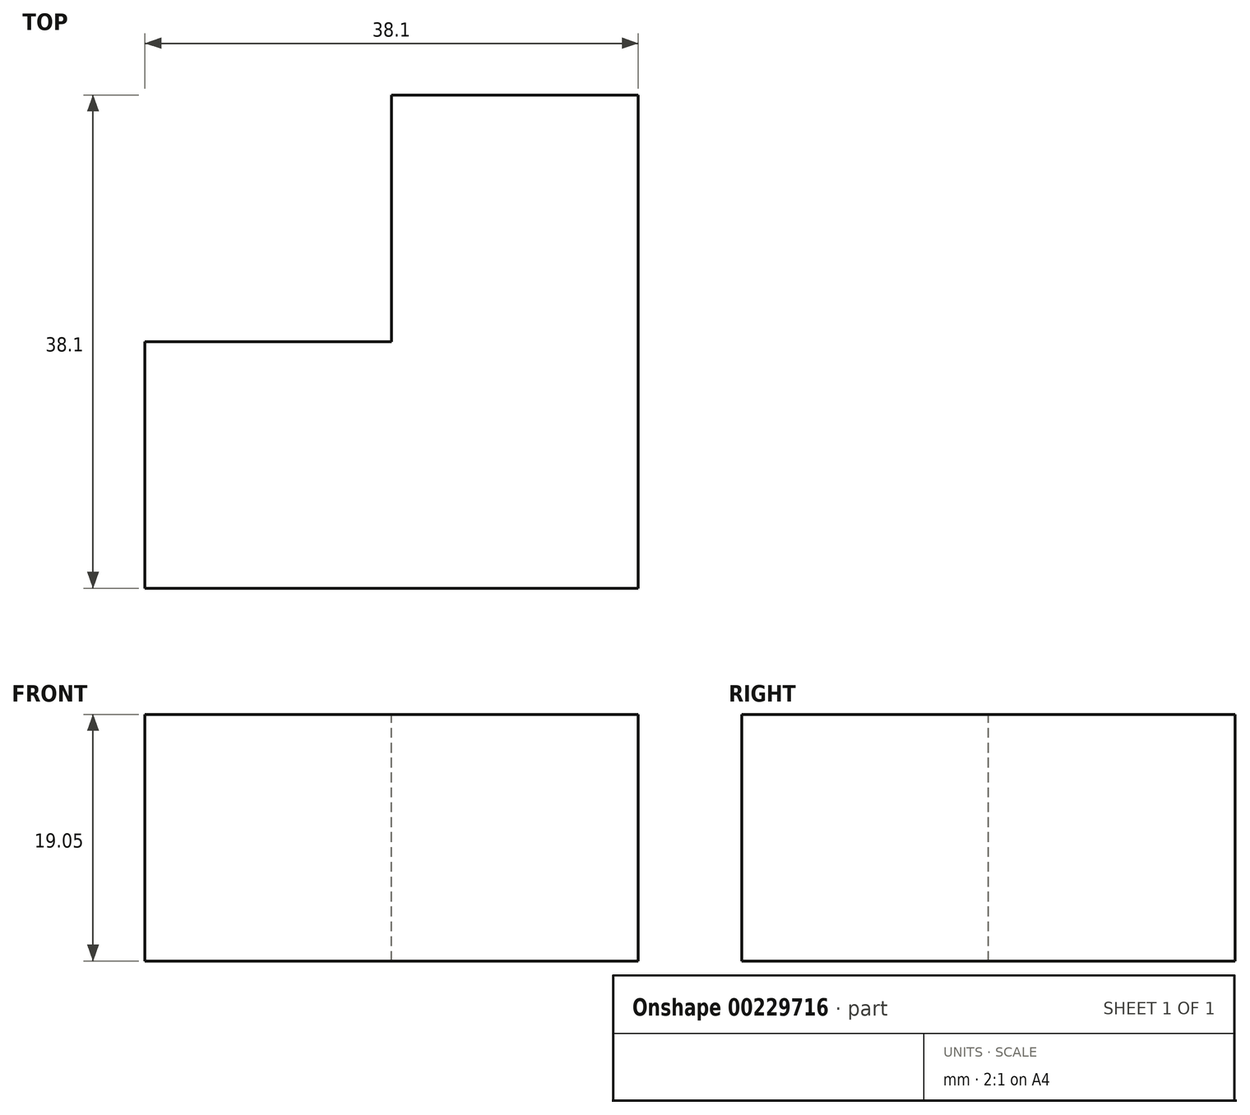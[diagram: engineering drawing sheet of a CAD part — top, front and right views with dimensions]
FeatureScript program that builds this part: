
annotation { "Feature Type Name" : "Feature", "Feature Type Description" : "" }
export const myFeature = defineFeature(function(context is Context, id is Id, definition is map)
    precondition{}
    {
        {
            var Q0;
            Q0=qCreatedBy(makeId("Front.planeOp"),FACE);
            var sketch = newSketch(context, id + "F0", { "sketchPlane" : qUnion([Q0])});
            skLineSegment(sketch, "E0.bottom", {"start": v(-44.5, 25.9) * mm, "end": v(-6.4, 25.9) * mm});
            skLineSegment(sketch, "E0.top", {"start": v(-44.5, 6.86) * mm, "end": v(-6.4, 6.86) * mm});
            skLineSegment(sketch, "E0.left", {"start": v(-44.5, 25.9) * mm, "end": v(-44.5, 6.86) * mm});
            skLineSegment(sketch, "E0.right", {"start": v(-6.4, 25.9) * mm, "end": v(-6.4, 6.86) * mm});
            skSolve(sketch);
        }
        {
            var Q0;
            Q0=makeQuery(id+"F0.imprint","IMPRINT",FACE,{"disambiguationData":[TD([[makeQuery(id+"F0.imprint","IMPRINT",EDGE,{"derivedFrom":sQuery(id+"F0.wireOp",EDGE,"E0.bottom")}),-1.0]])]});
            extrude(context, id + "F1", {"entities" : qUnion([Q0]), "depth" : 19.05 * mm});
        }
        {
            var Q0;
            Q0=makeQuery(id+"F1.opExtrude","SWEPT_FACE",FACE,{"disambiguationData":[OSD([sQuery(id+"F0.wireOp",EDGE,"E0.bottom")])]});
            var sketch = newSketch(context, id + "F2", { "sketchPlane" : qUnion([Q0])});
            skLineSegment(sketch, "E1.bottom", {"start": v(-6.4, 0) * mm, "end": v(-25.45, 0) * mm});
            skLineSegment(sketch, "E1.top", {"start": v(-6.4, 19.05) * mm, "end": v(-25.45, 19.05) * mm});
            skLineSegment(sketch, "E1.left", {"start": v(-6.4, 0) * mm, "end": v(-6.4, 19.05) * mm});
            skLineSegment(sketch, "E1.right", {"start": v(-25.45, 0) * mm, "end": v(-25.45, 19.05) * mm});
            skSolve(sketch);
        }
        {
            var Q0;
            Q0=makeQuery(id+"F2.imprint","IMPRINT",FACE,{"disambiguationData":[TD([[makeQuery(id+"F2.imprint","IMPRINT",EDGE,{"derivedFrom":sQuery(id+"F2.wireOp",EDGE,"E1.bottom")}),1.0]])]});
            extrude(context, id + "F3", {"entities" : qUnion([Q0]), "operationType" : NewBodyOperationType.ADD, "oppositeDirection" : true, "depth" : 19.05 * mm});
        }
    });
